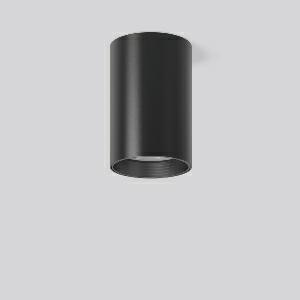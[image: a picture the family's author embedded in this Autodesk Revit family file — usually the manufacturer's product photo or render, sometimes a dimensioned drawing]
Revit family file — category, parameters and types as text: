
# Revit family: heledon_maxi_a_931229_003_2_2d08
name_source: partatom
category: Lighting Fixtures
units: mm (PartAtom-declared; Revit-internal decimal feet)

## family parameters
Cut with Voids When Loaded = No
Host = Face
Light Source = No
Part Type = Normal
Room Calculation Point = No
Round Connector Dimension = Use Diameter
Shared = No

## types (1)
- HELEDON maxi A (1 x LED Modul 927, 3450 lm, 2700)
    Apparent Load = 35 VA
    Approval mark = CE
    CIE Flux Codes = 96 100 100 100 100
    Color Rendering = 92
    Color Temperature = 2700
    Default Elevation = 1800 mm
    Description = Series: HELEDON maxi
Cylindrical surface-mounted downlight. Housing: die-cast aluminium, powder-coated. Internal ceiling frame polycarbonate with bayonet mounting. Black plastic ring and recessed LED to prevent glare from the side. Optical assembly with lens made of plastic (polycarbonate) for the best homogeneous light distribution - can be changed without tools. Best colour rendering index Ra>90. Suitable for Ceiling mounting. Easy installation with a separate ceiling frame with bayonet mounting and plug connection. Driver integrated. Connected via plug-in connector. High quality converter without flickering and stroboscopic effect. The following accessories can be mounted without use of tools: interchangeable lenses, decorative glasses, honeycomb louvre, clear and frosted diffusers, white interchangeable plastic ring. 
Colour: deep black, matt (RAL 9005)
Diameter: 123 mm
Height: 183 mm
Lamp: LED
Socket: without socket
Colour temperature: 2700K
Colour rendering index (CRI): 92
System power: 35 W
Rated luminous flux: 3450 lm
Luminous efficiency: 99 lm/W
Control gear: Regulated power supply
Protection class: I
Type of protection: IP 20
    Height = 183 mm
    Lamp = 1 x LED Modul 927
    Lamp Light Flux = 3450 lm
    Lamp count = 1
    Length = 123 mm
    Lifetime = 50000 h
    Luminous efficacy = 99 lm/W
    Manufacturer = RZB
    ModVariant = No
    Model = 931229.003.2
    Mounting Place = Ceiling
    Mounting Type = Surface mounted
    Number of Poles = 1
    OnlyDefault = Yes
    Power Factor = 1
    Product Name = HELEDON maxi A
    Product group = Surface mounted downlights
    ProductGroupID = 302
    Protection Class = Protection class I
    Protection Degree = IP 20
    RLX_Detail_Level = 1
    RLX_Emergency_Light_Flux = 0 lm
    RLX_Emergency_Type = 0
    RLX_Emergency_Type_DB = No
    RlxData = <blob elided: 97237 chars, md5=2813cc25>
    Socket = socket
    Standby Power = 0 W
    System Light Flux = 3450 lm
    System Power = 35 W
    Type Comments = Product without accessories
    Type Image = 931193.003.jpg
    URL = http://relux.com
    VarID = ---
    Voltage = 230 V
    Voltage Range = 220-240 V
    Weight = 0.00 kg
    Width = 0 mm  [stored 0 ft]

note: [stored X ft] marks values corroborated as IEEE doubles in the binary element streams (Revit-internal decimal feet)

## geometry (parser evidence)
native form markers: Blend x4, Sweep x12
no freeform markers — native parametric forms only
